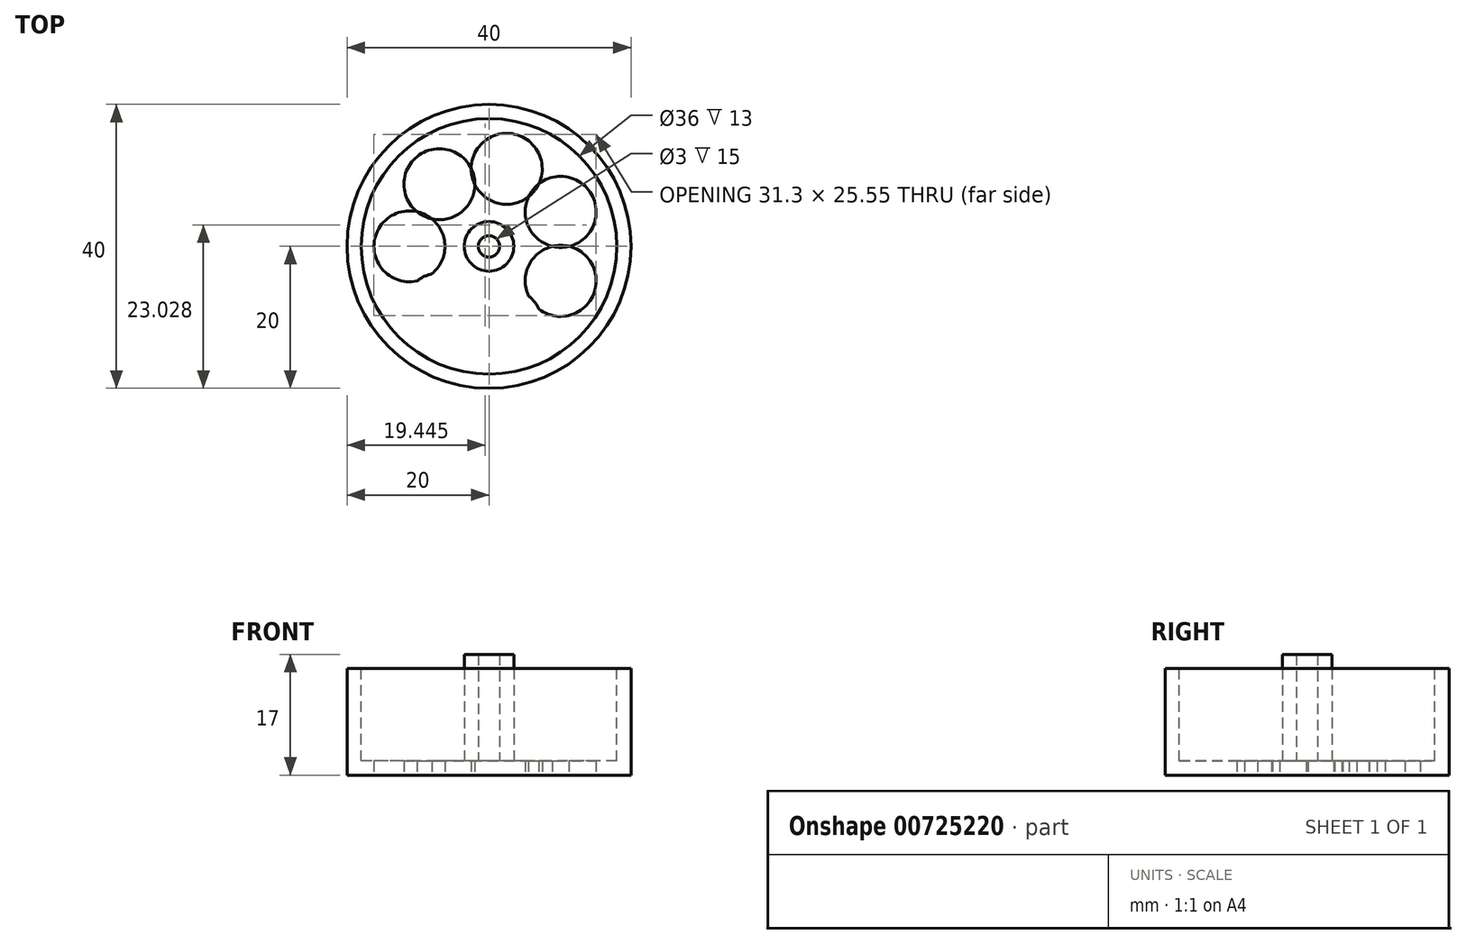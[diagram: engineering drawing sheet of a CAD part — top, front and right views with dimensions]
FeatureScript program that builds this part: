
annotation { "Feature Type Name" : "Feature", "Feature Type Description" : "" }
export const myFeature = defineFeature(function(context is Context, id is Id, definition is map)
    precondition{}
    {
        {
            var Q0;
            Q0=qCreatedBy(makeId("Top.planeOp"),FACE);
            var sketch = newSketch(context, id + "F0", { "sketchPlane" : qUnion([Q0])});
            skCircle(sketch, "E0", {"center": v(0, 0) * mm, "radius": 20 * mm});
            skSolve(sketch);
        }
        {
            var Q0;
            Q0=makeQuery(id+"F0.imprint","IMPRINT",FACE,{"disambiguationData":[TD([[makeQuery(id+"F0.imprint","IMPRINT",EDGE,{"derivedFrom":sQuery(id+"F0.wireOp",EDGE,"E0")}),1.0]])]});
            extrude(context, id + "F1", {"entities" : qUnion([Q0]), "depth" : 15 * mm, "offsetDistance" : 25 * mm});
        }
        {
            var Q0;
            Q0=makeQuery(id+"F1.opExtrude","CAP_FACE",FACE,{"disambiguationData":[OSD([sQuery(id+"F0.wireOp",EDGE,"E0")])],"isStart":false});
            var sketch = newSketch(context, id + "F2", { "sketchPlane" : qUnion([Q0])});
            skCircle(sketch, "E1", {"center": v(0, 0) * mm, "radius": 18 * mm});
            skSolve(sketch);
        }
        {
            var Q0;
            Q0=makeQuery(id+"F2.imprint","IMPRINT",FACE,{"disambiguationData":[TD([[makeQuery(id+"F2.imprint","IMPRINT",EDGE,{"derivedFrom":sQuery(id+"F2.wireOp",EDGE,"E1")}),1.0]])]});
            extrude(context, id + "F3", {"entities" : qUnion([Q0]), "operationType" : NewBodyOperationType.REMOVE, "oppositeDirection" : true, "depth" : 13 * mm, "offsetDistance" : 25 * mm});
        }
        {
            var Q0;
            Q0=makeQuery(id+"F3.boolean.opBoolean","COPY",FACE,{"derivedFrom":makeQuery(id+"F3.opExtrude","CAP_FACE",FACE,{"disambiguationData":[OSD([sQuery(id+"F2.wireOp",EDGE,"E1")])],"isStart":false})});
            var sketch = newSketch(context, id + "F4", { "sketchPlane" : qUnion([Q0])});
            skCircle(sketch, "E2", {"center": v(0, 0) * mm, "radius": 1.5 * mm});
            skCircle(sketch, "E3", {"center": v(0, 0) * mm, "radius": 3.5 * mm});
            skSolve(sketch);
        }
        {
            var Q0;
            Q0=makeQuery(id+"F4.imprint","IMPRINT",FACE,{"disambiguationData":[TD([[makeQuery(id+"F4.imprint","IMPRINT",EDGE,{"derivedFrom":sQuery(id+"F4.wireOp",EDGE,"E2")}),-1.0]])]});
            extrude(context, id + "F5", {"entities" : qUnion([Q0]), "operationType" : NewBodyOperationType.ADD, "depth" : 15 * mm, "offsetDistance" : 25 * mm});
        }
        {
            var Q0;
            Q0=makeQuery(id+"F1.opExtrude","CAP_FACE",FACE,{"disambiguationData":[OSD([sQuery(id+"F0.wireOp",EDGE,"E0")])],"isStart":true});
            var sketch = newSketch(context, id + "F6", { "sketchPlane" : qUnion([Q0])});
            skCircle(sketch, "E4", {"center": v(-11.2, 0) * mm, "radius": 5 * mm});
            skCircle(sketch, "E5.1.0", {"center": v(-6.99, -8.76) * mm, "radius": 5 * mm});
            skCircle(sketch, "E5.2.0", {"center": v(2.5, -10.92) * mm, "radius": 5 * mm});
            skCircle(sketch, "E5.3.0", {"center": v(10.1, -4.86) * mm, "radius": 5 * mm});
            skCircle(sketch, "E5.4.0", {"center": v(10.1, 4.86) * mm, "radius": 5 * mm});
            skPoint(sketch, "E5.center", {"position": v(0, 0) * mm});
            skCircle(sketch, "E6.1.5.0", {"center": v(2.5, 10.92) * mm, "radius": 5 * mm});
            skCircle(sketch, "E6.1.6.0", {"center": v(-6.99, 8.76) * mm, "radius": 5 * mm});
            skSolve(sketch);
        }
        {
            var Q0;
            Q0=makeQuery(id+"F6.imprint","IMPRINT",FACE,{"disambiguationData":[TD([[makeQuery(id+"F6.imprint","IMPRINT",EDGE,{"derivedFrom":sQuery(id+"F6.wireOp",EDGE,"E4")}),1.0]])]});
            var Q1;
            Q1=makeQuery(id+"F6.imprint","IMPRINT",FACE,{"disambiguationData":[TD([[makeQuery(id+"F6.imprint","IMPRINT",EDGE,{"derivedFrom":sQuery(id+"F6.wireOp",EDGE,"E5.4.0")}),1.0]])]});
            var Q2;
            Q2=makeQuery(id+"F6.imprint","IMPRINT",FACE,{"disambiguationData":[TD([[makeQuery(id+"F6.imprint","IMPRINT",EDGE,{"derivedFrom":sQuery(id+"F6.wireOp",EDGE,"E5.3.0")}),1.0]])]});
            var Q3;
            Q3=makeQuery(id+"F6.imprint","IMPRINT",FACE,{"disambiguationData":[TD([[makeQuery(id+"F6.imprint","IMPRINT",EDGE,{"derivedFrom":sQuery(id+"F6.wireOp",EDGE,"E5.2.0")}),1.0]])]});
            var Q4;
            Q4=makeQuery(id+"F6.imprint","IMPRINT",FACE,{"disambiguationData":[TD([[makeQuery(id+"F6.imprint","IMPRINT",EDGE,{"derivedFrom":sQuery(id+"F6.wireOp",EDGE,"E5.1.0")}),1.0]])]});
            var Q5;
            {var subQ0=sQuery(id+"F6.wireOp",EDGE,"9da88f8a-7587-4cf5-a4cb-777b40a140cb.1.6.0");var subQ1=sQuery(id+"F6.wireOp",EDGE,"E4");var subQ2=makeQuery(id+"F6.imprint","INTERSECT",VERTEX,{"disambiguationData":[OD(0.0)],"derivedFrom":[subQ1,subQ0]});Q5=makeQuery(id+"F6.imprint","IMPRINT",FACE,{"disambiguationData":[TD([[makeQuery(id+"F6.imprint","IMPRINT",EDGE,{"disambiguationData":[TD([[subQ2,-1.0]])],"derivedFrom":subQ1}),-1.0]])]});}
            var Q6;
            {var subQ0=sQuery(id+"F6.wireOp",EDGE,"9da88f8a-7587-4cf5-a4cb-777b40a140cb.1.5.0");var subQ1=sQuery(id+"F6.wireOp",EDGE,"E5.4.0");var subQ2=makeQuery(id+"F6.imprint","INTERSECT",VERTEX,{"disambiguationData":[OD(0.0)],"derivedFrom":[subQ1,subQ0]});Q6=makeQuery(id+"F6.imprint","IMPRINT",FACE,{"disambiguationData":[TD([[makeQuery(id+"F6.imprint","IMPRINT",EDGE,{"disambiguationData":[TD([[subQ2,1.0]])],"derivedFrom":subQ1}),-1.0]])]});}
            extrude(context, id + "F7", {"entities" : qUnion([Q0, Q1, Q2, Q3, Q4, Q5, Q6]), "operationType" : NewBodyOperationType.REMOVE, "oppositeDirection" : true, "depth" : 2 * mm, "offsetDistance" : 25 * mm});
        }
    });
